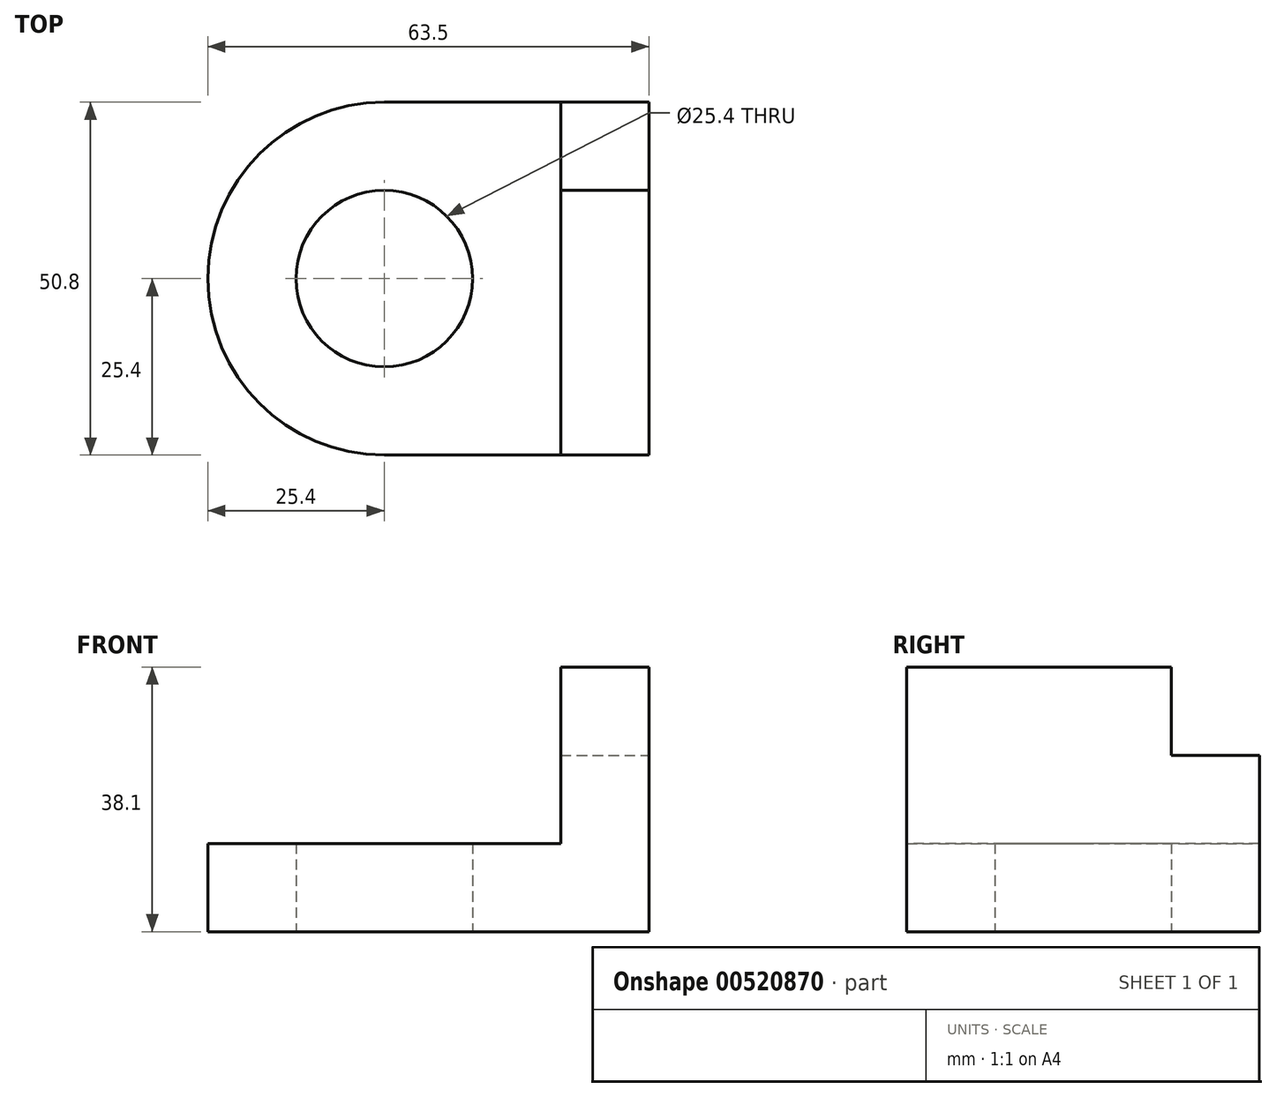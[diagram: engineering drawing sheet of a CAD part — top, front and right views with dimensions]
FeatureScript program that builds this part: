
annotation { "Feature Type Name" : "Feature", "Feature Type Description" : "" }
export const myFeature = defineFeature(function(context is Context, id is Id, definition is map)
    precondition{}
    {
        {
            var Q0;
            Q0=qCreatedBy(makeId("Top.planeOp"),FACE);
            var sketch = newSketch(context, id + "F0", { "sketchPlane" : qUnion([Q0])});
            skPoint(sketch, "E0.middle", {"position": v(25.4, 0) * mm});
            skCircle(sketch, "E1", {"center": v(0, 0) * mm, "radius": 25.4 * mm});
            skCircle(sketch, "E2", {"center": v(0, 0) * mm, "radius": 12.7 * mm});
            skLineSegment(sketch, "E3.bottom", {"start": v(0, 25.4) * mm, "end": v(38.1, 25.4) * mm});
            skLineSegment(sketch, "E3.top", {"start": v(0, -25.4) * mm, "end": v(38.1, -25.4) * mm});
            skLineSegment(sketch, "E3.left", {"start": v(0, 25.4) * mm, "end": v(0, -25.4) * mm});
            skLineSegment(sketch, "E3.right", {"start": v(38.1, 25.4) * mm, "end": v(38.1, -25.4) * mm});
            skSolve(sketch);
        }
        {
            var Q0;
            {var subQ0=sQuery(id+"F0.wireOp",EDGE,"E0.bottom");Q0=makeQuery(id+"F0.imprint","IMPRINT",FACE,{"disambiguationData":[TD([[makeQuery(id+"F0.imprint","IMPRINT",EDGE,{"derivedFrom":subQ0}),1.0]])]});}
            var Q1;
            {var subQ1=sQuery(id+"F0.wireOp",EDGE,"E0.right");var subQ3=sQuery(id+"F0.wireOp",EDGE,"E2");var subQ4=makeQuery(id+"F0.imprint","INTERSECT",VERTEX,{"disambiguationData":[OD(0.0)],"derivedFrom":[subQ1,subQ3]});Q1=makeQuery(id+"F0.imprint","IMPRINT",FACE,{"disambiguationData":[TD([[makeQuery(id+"F0.imprint","IMPRINT",EDGE,{"disambiguationData":[TD([[subQ4,-1.0]])],"derivedFrom":subQ3}),-1.0]])]});}
            var Q2;
            {var subQ1=sQuery(id+"F0.wireOp",EDGE,"E0.right");var subQ3=sQuery(id+"F0.wireOp",EDGE,"E2");var subQ4=makeQuery(id+"F0.imprint","INTERSECT",VERTEX,{"disambiguationData":[OD(0.0)],"derivedFrom":[subQ1,subQ3]});Q2=makeQuery(id+"F0.imprint","IMPRINT",FACE,{"disambiguationData":[TD([[makeQuery(id+"F0.imprint","IMPRINT",EDGE,{"disambiguationData":[TD([[subQ4,1.0]])],"derivedFrom":subQ3}),-1.0]])]});}
            extrude(context, id + "F1", {"entities" : qUnion([Q0, Q1, Q2]), "depth" : 12.7 * mm, "offsetDistance" : 25.4 * mm});
        }
        {
            var Q0;
            Q0 = qSketchRegion(id + "F0", true);
            extrude(context, id + "F2", {"entities" : qUnion([Q0]), "operationType" : NewBodyOperationType.ADD, "depth" : 12.7 * mm, "offsetDistance" : 25.4 * mm});
        }
        {
            var Q0;
            {var subQ0=sQuery(id+"F0.wireOp",EDGE,"E2");var subQ1=sQuery(id+"F0.wireOp",EDGE,"E1");Q0=makeQuery(id+"F2.boolean.opBoolean","MERGE",FACE,{"derivedFrom":[makeQuery(id+"F1.opExtrude","CAP_FACE",FACE,{"disambiguationData":[OSD([subQ1,subQ0])],"isStart":false}),makeQuery(id+"F2.opExtrude","CAP_FACE",FACE,{"disambiguationData":[OSD([subQ1,subQ0,sQuery(id+"F0.wireOp",EDGE,"E3.bottom"),sQuery(id+"F0.wireOp",EDGE,"E3.top"),sQuery(id+"F0.wireOp",EDGE,"E3.right")])],"isStart":false})]});}
            var sketch = newSketch(context, id + "F3", { "sketchPlane" : qUnion([Q0])});
            skLineSegment(sketch, "E4.bottom", {"start": v(38.1, -25.4) * mm, "end": v(25.4, -25.4) * mm});
            skLineSegment(sketch, "E4.top", {"start": v(38.1, 25.4) * mm, "end": v(25.4, 25.4) * mm});
            skLineSegment(sketch, "E4.left", {"start": v(38.1, -25.4) * mm, "end": v(38.1, 25.4) * mm});
            skLineSegment(sketch, "E4.right", {"start": v(25.4, -25.4) * mm, "end": v(25.4, 25.4) * mm});
            skSolve(sketch);
        }
        {
            var Q0;
            Q0=makeQuery(id+"F3.imprint","IMPRINT",FACE,{"disambiguationData":[TD([[makeQuery(id+"F3.imprint","IMPRINT",EDGE,{"derivedFrom":sQuery(id+"F3.wireOp",EDGE,"E4.bottom")}),1.0]])]});
            extrude(context, id + "F4", {"entities" : qUnion([Q0]), "operationType" : NewBodyOperationType.ADD, "depth" : 25.4 * mm, "offsetDistance" : 25.4 * mm});
        }
        {
            var Q0;
            Q0=makeQuery(id+"F4.opExtrude","CAP_FACE",FACE,{"disambiguationData":[OSD([sQuery(id+"F3.wireOp",EDGE,"E4.bottom"),sQuery(id+"F3.wireOp",EDGE,"E4.top"),sQuery(id+"F3.wireOp",EDGE,"E4.left"),sQuery(id+"F3.wireOp",EDGE,"E4.right")])],"isStart":false});
            var sketch = newSketch(context, id + "F5", { "sketchPlane" : qUnion([Q0])});
            skLineSegment(sketch, "E5.bottom", {"start": v(25.4, 25.4) * mm, "end": v(38.1, 25.4) * mm});
            skLineSegment(sketch, "E5.top", {"start": v(25.4, 12.7) * mm, "end": v(38.1, 12.7) * mm});
            skLineSegment(sketch, "E5.left", {"start": v(25.4, 25.4) * mm, "end": v(25.4, 12.7) * mm});
            skLineSegment(sketch, "E5.right", {"start": v(38.1, 25.4) * mm, "end": v(38.1, 12.7) * mm});
            skSolve(sketch);
        }
        {
            var Q0;
            Q0=makeQuery(id+"F5.imprint","IMPRINT",FACE,{"disambiguationData":[TD([[makeQuery(id+"F5.imprint","IMPRINT",EDGE,{"derivedFrom":sQuery(id+"F5.wireOp",EDGE,"E5.bottom")}),-1.0]])]});
            extrude(context, id + "F6", {"entities" : qUnion([Q0]), "operationType" : NewBodyOperationType.REMOVE, "oppositeDirection" : true, "depth" : 12.7 * mm, "offsetDistance" : 25.4 * mm});
        }
    });
